# Revit family: Sanitary_Toilets_Sanindusa_Urby-Plus_Close-coupled-Toilet-With-Hole-For-Water-Supply
name_source: partatom
category: Plumbing Fixtures
revit_build: Autodesk Revit 2018 (Build: 20170223_1515(x64)
units: mm (PartAtom-declared; Revit-internal decimal feet)

## family parameters
Cut with Voids When Loaded = No
Host = Face
Part Type = Normal
Room Calculation Point = No
Round Connector Dimension = Use Diameter
Shared = No

## types (1)
- Sanitary_Toilets_Sanindusa_Urby-Plus_Close-coupled-Toilet-With-Hole-For-Water-Supply
    AssetType = Fixed
    CodePerformance = EN 997:2012 CL 1 - 6 A
    Color = white
    Constituents = Compatible toilet seats (not included): 2401100-Urby toilet seat with clipoff system; 24031-Urby toilet seat with clipoff and slowclose system. Compatible cisterns (not included): 140171004LM - Urby60 bottom water supply connection cistern with dual flush mechanism; 140173004LM - Urby60 side water supply connection cistern with dual flush mechanism. 23-fixing kit (included)
    Default Elevation = 1219 mm
    Description = Soil appliance for the disposal of excrement.
    DrainSize = 90 mm  [stored 0.295276 ft]
    Element Type = TOILETPAN: Soil appliance for the disposal of excrement.
    Features = Domestic and commercial use. Versatile timeless design. Seats with clipoff system easy to clean and slow close option. Back to wall WC.
    Finish = gloss
    Installation Instructions = https://www.tec.sanindusa.pt
    InstallationDate = 1900-12-31T23:59:59
    Manufacturer = Sanindusa
    ManufacturerName = Sanindusa
    ManufacturerURL = www.tec.sanindusa.pt
    Material = vitreous china
    Model = 146024004
    ModelNumber = 146024004
    ModelReference = Urby Plus
    Name = Urb.y plus F|D close coupled toilet
    NominalHeight = 840 mm  [stored 2.75591 ft]
    NominalLength = 379 mm  [stored 1.24344 ft]
    NominalWidth = 590 mm  [stored 1.9357 ft]
    PanColor = white
    PanMaterial = vitreous china
    PanMounting = backtowall
    Pre-defined type (IFC) = TOILETPAN
    ProductInformation = https://www.tec.sanindusa.pt
    ProductionYear = 2019
    Size = 379x590x840
    ToiletPanType = washdown
    ToiletType = CloseCoupled
    Type (IFC) = IfcSanitaryTerminalType
    URL = www.tec.sanindusa.pt
    Uniclass2015Code = Pr_40_20_93_94
    Uniclass2015Title = WC pans
    Uniclass2015Version = Products v1.6
    Version = 1
    WarrantyDescription = https://www.tec.sanindusa.pt
    WarrantyDurationParts = 5
    WarrantyDurationUnit = year
    WarrantyStartDate = 1900-12-31T23:59:59
    Waste Connection = Yes
    Weight = 35.20 kg

note: [stored X ft] marks values corroborated as IEEE doubles in the binary element streams (Revit-internal decimal feet)

## geometry (parser evidence)
native form markers: Sweep x5
no freeform markers — native parametric forms only
